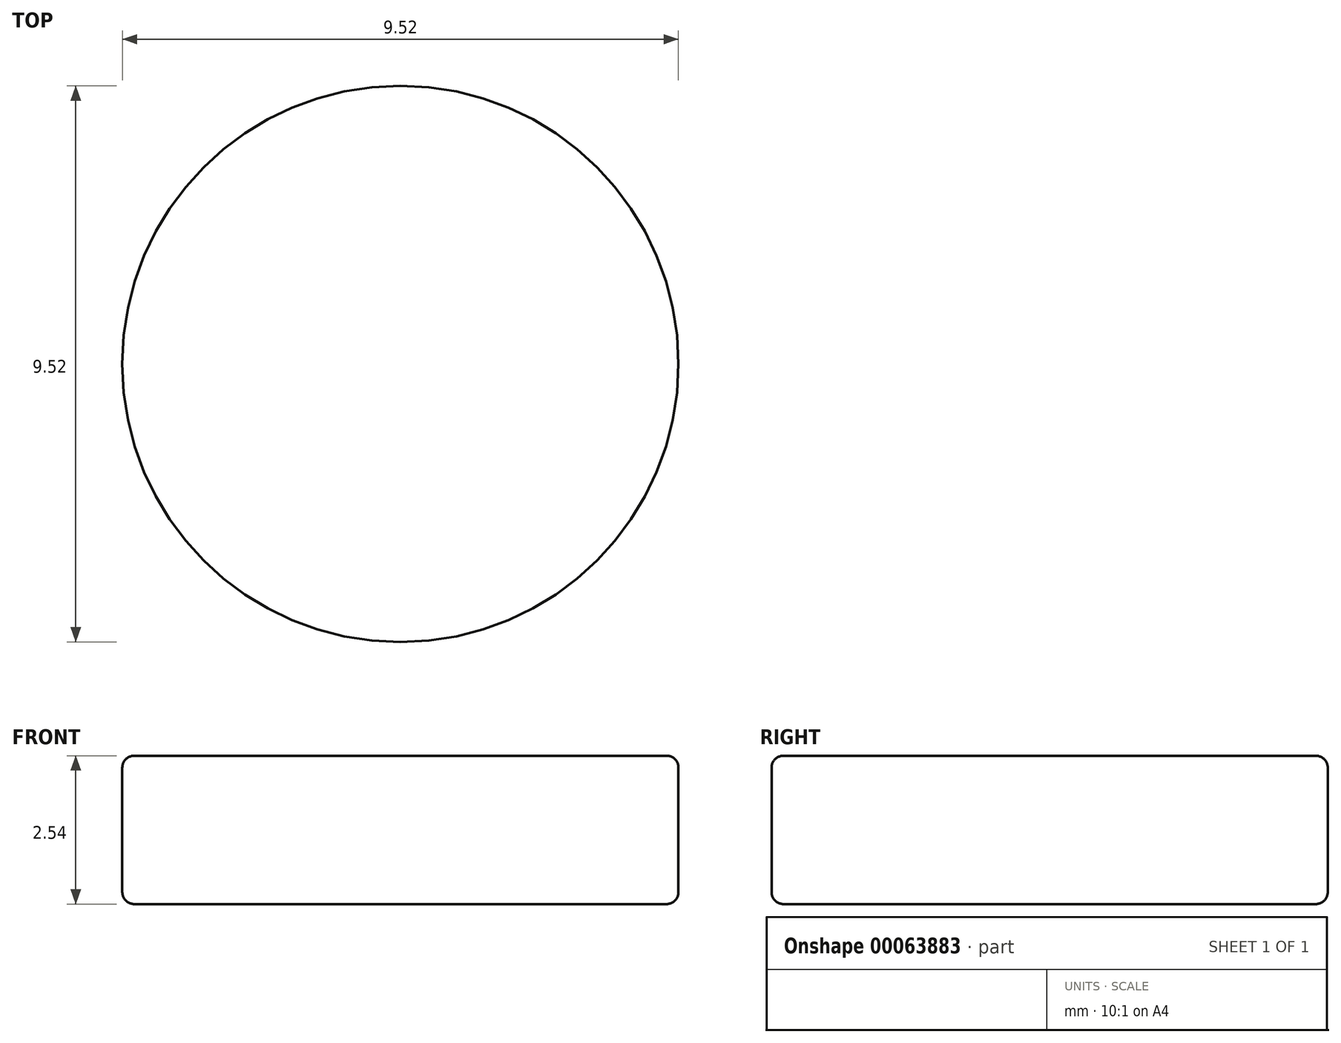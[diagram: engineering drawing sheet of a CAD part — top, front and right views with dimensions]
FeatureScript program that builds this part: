
annotation { "Feature Type Name" : "Feature", "Feature Type Description" : "" }
export const myFeature = defineFeature(function(context is Context, id is Id, definition is map)
    precondition{}
    {
        {
            var Q0;
            Q0=qCreatedBy(makeId("Top.planeOp"),FACE);
            var sketch = newSketch(context, id + "F0", { "sketchPlane" : qUnion([Q0])});
            skCircle(sketch, "E0", {"center": v(0, 0) * mm, "radius": 4.76 * mm});
            skSolve(sketch);
        }
        {
            var Q0;
            Q0=makeQuery(id+"F0.imprint","IMPRINT",FACE,{"disambiguationData":[TD([[makeQuery(id+"F0.imprint","IMPRINT",EDGE,{"derivedFrom":sQuery(id+"F0.wireOp",EDGE,"E0")}),1.0]])]});
            extrude(context, id + "F1", {"entities" : qUnion([Q0]), "depth" : 2.54 * mm});
        }
        {
            var Q0;
            Q0=makeQuery(id+"F1.opExtrude","SWEPT_FACE",FACE,{"disambiguationData":[OSD([sQuery(id+"F0.wireOp",EDGE,"E0")])]});
            fillet(context, id + "F2", {"entities" : qUnion([Q0]), "radius" : 0.2 * mm, "tangentPropagation" : true, "allowEdgeOverflow" : false});
        }
    });
